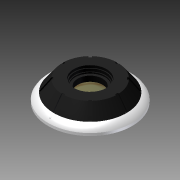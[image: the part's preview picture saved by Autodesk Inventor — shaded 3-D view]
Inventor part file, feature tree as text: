
AUTODESK INVENTOR PART (.ipt)
format: ipt  version: 2011 (Build 150239000, 239)  size: 235,008 bytes
history: native  units: in
note: dims shown in document units (in); Inventor stores cm internally (conversion verified against a paired STEP export)
features: sketch x11, extrude x6, revolve x3, plane x3, projected_geometry x3, loft x1, pattern_circular x1
ambient origin geometry x8: Origin, YZ Plane, XZ Plane, XY Plane, X Axis, Y Axis, Z Axis, Center Point
bodies: Solid1 (feature_tree)
feature tree (28):
  revolve  "Revolution1"  [1 undecoded]
  plane  "Work Plane2"
  revolve  "Revolution2"  [1 undecoded]
  sketch  "Sketch3"  dims[d8=90.0deg d9=0.02in]
  plane  "Work Plane3"
  loft  "Loft1"
  pattern_circular  "Circular Pattern1"  Count=8 Angle=90.0deg
  extrude  "Extrusion1"  Depth=0.175in TaperAngle=0.0deg
  extrude  "Extrusion2"  Depth=0.375in
  extrude  "Extrusion3"  Depth=0.08in TaperAngle=0.0deg
  extrude  "Extrusion4"  Depth=0.02in TaperAngle=0.0deg
  extrude  "Extrusion5"  Depth=0.02in TaperAngle=0.0deg
  revolve  "Revolution3"  [1 undecoded]
  extrude  "Extrusion6"  TaperAngle=90.0deg  [1 undecoded]
  sketch  "Sketch1"  dims[d2=0.125in d3=0.5475in]
  plane  "Work Plane1"
  sketch  "Sketch2"  dims[d5=90.0deg d6=0.0625in d7=0.02in]
  projected_geometry  "Projected Loop1"
  projected_geometry  "Projected Loop2"
  sketch  "Sketch4"  dims[d10=0.02in]
  projected_geometry  "Projected Loop3"
  sketch  "Sketch5"  dims[d11=0.02in]
  sketch  "Sketch6"  dims[d12=0.04in]
  sketch  "Sketch7"  dims[d13=0.125in]
  sketch  "Sketch8"  dims[d14=0.02in]
  sketch  "Sketch9"  dims[d15=0.04in]
  sketch  "Sketch10"  dims[d16=0.0in d17=90.0deg d18=0.0in d19=90.0deg d20=3.1496in d21=360.0deg]
  sketch  "Sketch11"  dims[d23=0.495in d24=0.175in d25=0.0in d26=0.375in d27=0.08in d28=0.0in d29=0.02in d30=0.0in d31=0.02in d32=0.0in d33=0.02in d34=0.0in d35=90.0deg d36=1.0in d37=0.0in]
note: 4 required parameter values undecoded (feature->parameter linkage not recoverable at this tier; creation-order binding heuristic only, values carry confidence <= 0.55)